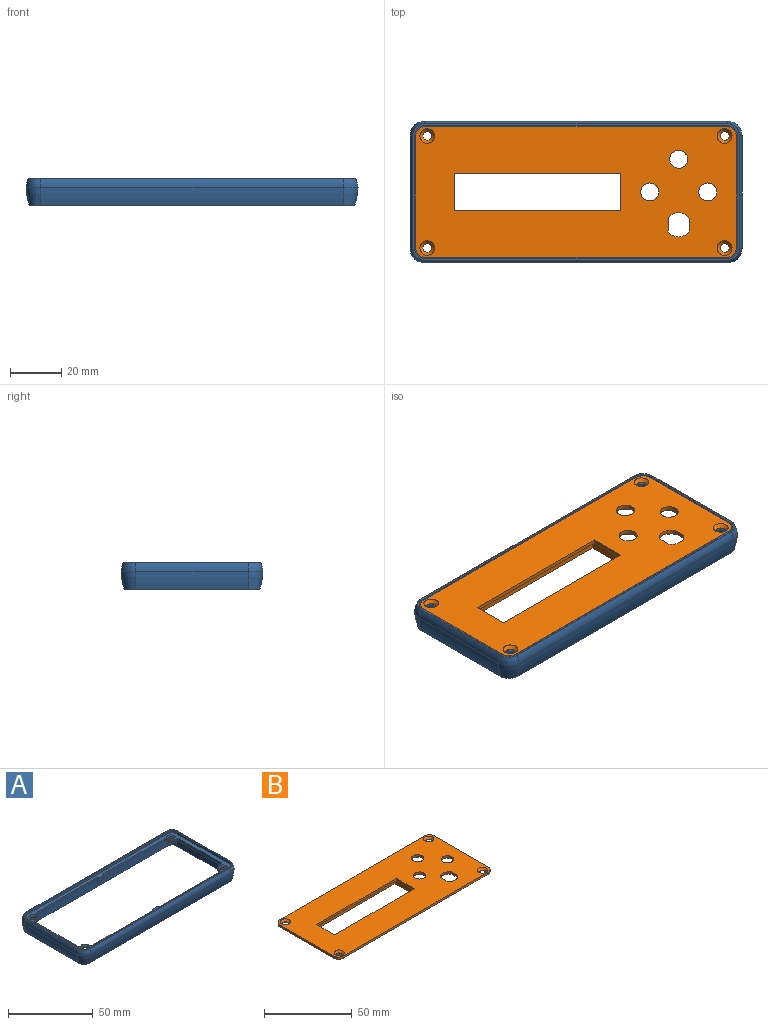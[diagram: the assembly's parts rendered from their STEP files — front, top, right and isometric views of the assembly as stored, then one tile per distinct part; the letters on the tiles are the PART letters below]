
ASSEMBLY  parts=2 mates=1
PART A: 104 faces, bbox 129.9x56.1x10.5 mm
  f0: torus R=5.55mm, axis (0,0,-1), area 0.1mm2, adj f4,f5,f68,f77
  f1: torus R=5.55mm, axis (0,0,-1), area 0.1mm2, adj f4,f6,f66,f94
  f2: torus R=5.55mm, axis (0,0,-1), area 0.1mm2, adj f5,f7,f75,f87
  f3: torus R=5.55mm, axis (0,0,-1), area 0.1mm2, adj f6,f7,f79,f90
  f4: cylinder r=0.2mm len=117.5mm, axis (1,0,0), area 1.3mm2, adj f0,f1,f67,f97
  f5: cylinder r=0.2mm len=43.63mm, axis (0,1,0), area 0.5mm2, adj f0,f2,f76,f102
  f6: cylinder r=0.2mm len=43.63mm, axis (0,-1,0), area 0.5mm2, adj f1,f3,f65,f92
  f7: cylinder r=0.2mm len=117.5mm, axis (-1,0,0), area 1.3mm2, adj f2,f3,f74,f80
  f8: cylinder r=0.2mm len=43.63mm, axis (0,-1,0), area 9.2mm2, adj f72,f73,f78,f92
  f9: cylinder r=0.2mm len=117.5mm, axis (-1,0,0), area 24.7mm2, adj f71,f73,f74,f78
  f10: cylinder r=0.2mm len=117.5mm, axis (1,0,0), area 24.7mm2, adj f70,f72,f78,f97
  f11: cylinder r=0.2mm len=43.63mm, axis (0,1,0), area 9.2mm2, adj f70,f71,f76,f78
  f12: cylinder r=0.2mm len=43.63mm, axis (0,-1,0), area 11mm2, adj f63,f64,f65,f69
  f13: cylinder r=0.2mm len=117.5mm, axis (-1,0,0), area 29.5mm2, adj f62,f64,f69,f80
  f14: cylinder r=0.2mm len=117.5mm, axis (1,0,0), area 29.5mm2, adj f61,f63,f67,f69
  f15: cylinder r=0.2mm len=43.63mm, axis (0,1,0), area 11mm2, adj f61,f62,f69,f102
  f16: cylinder r=1mm len=1.8mm, axis (0,0,-1), area 2.8mm2, adj f32,f54,f56,f85
  f17: cylinder r=1mm len=1.8mm, axis (0,0,1), area 2.8mm2, adj f32,f49,f55,f85
  f18: cylinder r=1mm len=1.8mm, axis (0,0,-1), area 2.8mm2, adj f32,f48,f55,f85
  f19: cylinder r=1mm len=1.8mm, axis (0,0,1), area 2.8mm2, adj f32,f45,f56,f85
  f20: cylinder r=1mm len=3mm, axis (0,0,-1), area 4.7mm2, adj f32,f35,f36,f37,f39
  f21: cylinder r=1mm len=3mm, axis (0,0,-1), area 4.7mm2, adj f32,f35,f36,f37,f40
  f22: cylinder r=1mm len=3mm, axis (0,0,-1), area 4.7mm2, adj f32,f33,f34,f38,f41
  f23: cylinder r=1mm len=3mm, axis (0,0,-1), area 4.7mm2, adj f32,f33,f34,f38,f42
  f24: cylinder r=1.75mm len=3.5mm, axis (0,0,-1), area 11.5mm2, adj f25,f85
  f25: cone r=2.12mm half-angle=45deg, axis (0,0,1), area 14.2mm2, adj f24,f32
  f26: cylinder r=1.75mm len=3.5mm, axis (0,0,-1), area 11.5mm2, adj f27,f85
  f27: cone r=2.12mm half-angle=45deg, axis (0,0,1), area 14.2mm2, adj f26,f32
  f28: cylinder r=1.75mm len=3.5mm, axis (0,0,-1), area 11.5mm2, adj f29,f85
  f29: cone r=2.12mm half-angle=45deg, axis (0,0,1), area 14.2mm2, adj f28,f32
  f30: cylinder r=1.75mm len=3.5mm, axis (0,0,-1), area 11.5mm2, adj f31,f85
  f31: cone r=2.12mm half-angle=45deg, axis (0,0,1), area 14.2mm2, adj f30,f32
  f32: plane 125.5x51.63mm, normal (0,0,1), area 816.8mm2, adj f16,f17,f18,f19,f20,f21,f22,f23
  f33: plane 5x1mm, normal (0,0,-1), area 4.6mm2, adj f22,f23,f34,f38
  f34: plane 3x3mm, normal (0,1,0), area 9mm2, adj f22,f23,f32,f33
  f35: plane 5x1mm, normal (0,0,-1), area 4.6mm2, adj f20,f21,f36,f37
  f36: plane 3x3mm, normal (0,-1,0), area 9mm2, adj f20,f21,f32,f35
  f37: plane 5x1.2mm, normal (0,1,0), area 6mm2, adj f20,f21,f35,f85
  f38: plane 5x1.2mm, normal (0,-1,0), area 6mm2, adj f22,f23,f33,f85
  f39: plane 51.26x1.8mm, normal (0,-1,0), area 92.3mm2, adj f20,f32,f50,f85
  f40: plane 51.26x1.8mm, normal (0,-1,0), area 92.3mm2, adj f21,f32,f43,f85
  f41: plane 51.26x1.8mm, normal (0,1,0), area 92.3mm2, adj f22,f32,f46,f85
  f42: plane 51.26x1.8mm, normal (0,1,0), area 92.3mm2, adj f23,f32,f52,f85
  f43: cylinder r=1mm len=1.8mm, axis (0,0,-1), area 2.8mm2, adj f32,f40,f44,f85
  f44: plane 1.8x0.81mm, normal (1,0,0), area 1.4mm2, adj f32,f43,f84,f85
  f45: plane 1.8x1.49mm, normal (0,1,0), area 2.7mm2, adj f19,f32,f81,f85
  f46: cylinder r=1mm len=1.8mm, axis (0,0,1), area 2.8mm2, adj f32,f41,f47,f85
  f47: plane 1.8x0.81mm, normal (1,0,0), area 1.4mm2, adj f32,f46,f82,f85
  f48: plane 1.8x1.49mm, normal (0,1,0), area 2.7mm2, adj f18,f32,f82,f85
  f49: plane 1.8x1.49mm, normal (0,-1,0), area 2.7mm2, adj f17,f32,f84,f85
  f50: cylinder r=1mm len=1.8mm, axis (0,0,1), area 2.8mm2, adj f32,f39,f51,f85
  f51: plane 1.8x0.81mm, normal (-1,0,0), area 1.4mm2, adj f32,f50,f83,f85
  f52: cylinder r=1mm len=1.8mm, axis (0,0,-1), area 2.8mm2, adj f32,f42,f53,f85
  f53: plane 1.8x0.81mm, normal (-1,0,0), area 1.4mm2, adj f32,f52,f81,f85
  f54: plane 1.8x1.49mm, normal (0,-1,0), area 2.7mm2, adj f16,f32,f83,f85
  f55: plane 35.52x1.8mm, normal (1,0,0), area 63.9mm2, adj f17,f18,f32,f85
  f56: plane 35.52x1.8mm, normal (-1,0,0), area 63.9mm2, adj f16,f19,f32,f85
  f57: cylinder r=4mm len=4mm, axis (0,0,-1), area 10.7mm2, adj f32,f58,f78,f96
  f58: plane 43.63x1.7mm, normal (-1,0,0), area 74.2mm2, adj f32,f57,f59,f78
  f59: cylinder r=4mm len=4mm, axis (0,0,-1), area 10.7mm2, adj f32,f58,f60,f78
  f60: plane 117.5x1.7mm, normal (0,1,0), area 199.8mm2, adj f32,f59,f78,f86
  f61: torus R=4.36mm, axis (0,0,-1), area 1.8mm2, adj f14,f15,f68,f69
  f62: torus R=4.36mm, axis (0,0,-1), area 1.8mm2, adj f13,f15,f69,f87
  f63: torus R=4.36mm, axis (0,0,-1), area 1.8mm2, adj f12,f14,f66,f69
  f64: torus R=4.36mm, axis (0,0,-1), area 1.8mm2, adj f12,f13,f69,f79
  f65: cylinder r=25mm len=43.63mm, axis (0,-1,0), area 304.7mm2, adj f6,f12,f66,f79
  f66: revolved ~6.86x5.75mm, area 58.2mm2, adj f1,f63,f65,f67
  f67: cylinder r=25mm len=117.5mm, axis (1,0,0), area 820.6mm2, adj f4,f14,f66,f68
  f68: revolved ~6.86x5.75mm, area 58.2mm2, adj f0,f61,f67,f102
  f69: plane 126.21x52.34mm, normal (0,0,-1), area 123.7mm2, adj f12,f13,f14,f15,f61,f62,f63,f64
  f70: torus R=4.63mm, axis (0,0,-1), area 1.6mm2, adj f10,f11,f77,f78
  f71: torus R=4.63mm, axis (0,0,-1), area 1.6mm2, adj f9,f11,f75,f78
  f72: torus R=4.63mm, axis (0,0,-1), area 1.6mm2, adj f8,f10,f78,f94
  f73: torus R=4.63mm, axis (0,0,-1), area 1.6mm2, adj f8,f9,f78,f90
  f74: cylinder r=7.19mm len=117.5mm, axis (-1,0,0), area 418mm2, adj f7,f9,f75,f90
  f75: revolved ~5.75x5.75mm, area 30.3mm2, adj f2,f71,f74,f76
  f76: cylinder r=7.19mm len=43.63mm, axis (0,1,0), area 155.2mm2, adj f5,f11,f75,f77
  f77: revolved ~5.75x5.75mm, area 30.3mm2, adj f0,f70,f76,f97
  f78: plane 126.77x52.9mm, normal (0,0,1), area 221.8mm2, adj f8,f9,f10,f11,f57,f58,f59,f60
  f79: revolved ~6.86x5.75mm, area 58.2mm2, adj f3,f64,f65,f80
  f80: cylinder r=25mm len=117.5mm, axis (-1,0,0), area 820.6mm2, adj f7,f13,f79,f87
  f81: cylinder r=3mm len=3mm, axis (0,0,-1), area 8.5mm2, adj f32,f45,f53,f85
  f82: cylinder r=3mm len=3mm, axis (0,0,-1), area 8.5mm2, adj f32,f47,f48,f85
  f83: cylinder r=3mm len=3mm, axis (0,0,-1), area 8.5mm2, adj f32,f51,f54,f85
  f84: cylinder r=3mm len=3mm, axis (0,0,-1), area 8.5mm2, adj f32,f44,f49,f85
  f85: plane 125.5x51.63mm, normal (0,0,-1), area 847.7mm2, adj f16,f17,f18,f19,f24,f26,f28,f30
  f86: cylinder r=4mm len=4mm, axis (0,0,-1), area 10.7mm2, adj f32,f60,f78,f101
  f87: revolved ~6.86x5.75mm, area 58.2mm2, adj f2,f62,f80,f102
  f88: cylinder r=4mm len=7mm, axis (0,0,-1), area 44mm2, adj f69,f85,f89,f103
  f89: plane 117.5x7mm, normal (0,1,0), area 822.5mm2, adj f69,f85,f88,f91
  f90: revolved ~5.75x5.75mm, area 30.3mm2, adj f3,f73,f74,f92
  f91: cylinder r=4mm len=7mm, axis (0,0,-1), area 44mm2, adj f69,f85,f89,f93
  f92: cylinder r=7.19mm len=43.63mm, axis (0,-1,0), area 155.2mm2, adj f6,f8,f90,f94
  f93: plane 43.63x7mm, normal (-1,0,0), area 305.4mm2, adj f69,f85,f91,f95
  f94: revolved ~5.75x5.75mm, area 30.3mm2, adj f1,f72,f92,f97
  f95: cylinder r=4mm len=7mm, axis (0,0,-1), area 44mm2, adj f69,f85,f93,f98
  f96: plane 117.5x1.7mm, normal (0,-1,0), area 199.8mm2, adj f32,f57,f78,f99
  f97: cylinder r=7.19mm len=117.5mm, axis (1,0,0), area 418mm2, adj f4,f10,f77,f94
  f98: plane 117.5x7mm, normal (0,-1,0), area 822.5mm2, adj f69,f85,f95,f100
  f99: cylinder r=4mm len=4mm, axis (0,0,-1), area 10.7mm2, adj f32,f78,f96,f101
  f100: cylinder r=4mm len=7mm, axis (0,0,-1), area 44mm2, adj f69,f85,f98,f103
  f101: plane 43.63x1.7mm, normal (1,0,0), area 74.2mm2, adj f32,f78,f86,f99
  f102: cylinder r=25mm len=43.63mm, axis (0,1,0), area 304.7mm2, adj f5,f15,f68,f87
  f103: plane 43.63x7mm, normal (1,0,0), area 305.4mm2, adj f69,f85,f88,f100
PART B: 82 faces, bbox 124.8x50.9x8 mm
  f0: plane 10.05x4mm, normal (1,0,0), area 40.2mm2, adj f56,f59,f75,f81
  f1: plane 71.5x24mm, normal (0,0,-1), area 780.8mm2, adj f28,f29,f30,f31,f43,f67,f68,f69
  f2: plane 0.49x0.01mm, normal (0,0,-1), area 0mm2, adj f44,f65
  f3: plane 1.2x0.12mm, normal (0,0,-1), area 0.1mm2, adj f5,f58
  f4: plane 13x12.9mm, normal (0,0,-1), area 93.5mm2, adj f34,f42,f61,f80,f81
  f5: cylinder r=2.5mm len=2.5mm, axis (0,0,1), area 2.9mm2, adj f3,f56,f58
  f6: cylinder r=2.5mm len=2.5mm, axis (0,0,1), area 1.2mm2, adj f56,f57
  f7: plane 13x13mm, normal (0,0,-1), area 94.2mm2, adj f33,f53
  f8: plane 124.8x50.9mm, normal (0,0,-1), area 1172.2mm2, adj f13,f15,f17,f19,f20,f21,f22,f23
  f9: plane 13x13mm, normal (0,0,-1), area 94.2mm2, adj f32,f52
  f10: plane 15.5x14.2mm, normal (0,0,-1), area 116.6mm2, adj f35,f36,f37,f38,f39,f40,f41,f55
  f11: plane 124.8x50.9mm, normal (0,0,1), area 5117.3mm2, adj f12,f14,f16,f18,f20,f21,f22,f23
  f12: cone r=2.31mm half-angle=41deg, axis (0,0,1), area 24.9mm2, adj f11,f13
  f13: cylinder r=1.75mm len=3.5mm, axis (0,0,1), area 1.7mm2, adj f8,f12
  f14: cone r=2.31mm half-angle=41deg, axis (0,0,1), area 24.9mm2, adj f11,f15
  f15: cylinder r=1.75mm len=3.5mm, axis (0,0,1), area 1.7mm2, adj f8,f14
  f16: cone r=2.31mm half-angle=41deg, axis (0,0,1), area 24.9mm2, adj f11,f17
  f17: cylinder r=1.75mm len=3.5mm, axis (0,0,1), area 1.7mm2, adj f8,f16
  f18: cone r=2.31mm half-angle=41deg, axis (0,0,1), area 24.9mm2, adj f11,f19
  f19: cylinder r=1.75mm len=3.5mm, axis (0,0,1), area 1.7mm2, adj f8,f18
  f20: plane 42.9x1.45mm, normal (-1,0,0), area 62.2mm2, adj f8,f11,f21,f27
  f21: cylinder r=4mm len=4mm, axis (0,0,-1), area 9.1mm2, adj f8,f11,f20,f22
  f22: plane 116.8x1.45mm, normal (0,-1,0), area 169.4mm2, adj f8,f11,f21,f23
  f23: cylinder r=4mm len=4mm, axis (0,0,-1), area 9.1mm2, adj f8,f11,f22,f24
  f24: plane 42.9x1.45mm, normal (1,0,0), area 62.2mm2, adj f8,f11,f23,f25
  f25: cylinder r=4mm len=4mm, axis (0,0,-1), area 9.1mm2, adj f8,f11,f24,f26
  f26: plane 116.8x1.45mm, normal (0,1,0), area 169.4mm2, adj f8,f11,f25,f27
  f27: cylinder r=4mm len=4mm, axis (0,0,-1), area 9.1mm2, adj f8,f11,f20,f26
  f28: plane 64.5x1.45mm, normal (0,1,0), area 93.5mm2, adj f1,f11,f29,f31
  f29: plane 14.5x1.45mm, normal (1,0,0), area 21mm2, adj f1,f11,f28,f30
  f30: plane 64.5x1.45mm, normal (0,-1,0), area 93.5mm2, adj f1,f11,f29,f31
  f31: plane 14.5x1.45mm, normal (-1,0,0), area 21mm2, adj f1,f11,f28,f30
  f32: cylinder r=3.5mm len=7mm, axis (0,0,1), area 31.9mm2, adj f9,f11
  f33: cylinder r=3.5mm len=7mm, axis (0,0,1), area 31.9mm2, adj f7,f11
  f34: cylinder r=3.5mm len=7mm, axis (0,0,1), area 31.9mm2, adj f4,f11
  f35: plane 4.8x1.45mm, normal (1,0,0), area 7mm2, adj f10,f11,f36,f38
  f36: cylinder r=4.75mm len=8.2mm, axis (0,0,1), area 14.3mm2, adj f10,f11,f35,f37
  f37: plane 4.8x1.45mm, normal (-1,0,0), area 7mm2, adj f10,f11,f36,f38
  f38: cylinder r=4.75mm len=8.2mm, axis (0,0,1), area 14.3mm2, adj f10,f11,f35,f37
  f39: plane 6.21x2.5mm, normal (-1,0,0), area 15.5mm2, adj f10,f40,f55,f56
  f40: cylinder r=7.75mm len=14.2mm, axis (0,0,1), area 44.9mm2, adj f10,f39,f41,f56
  f41: plane 6.21x2.5mm, normal (1,0,0), area 15.5mm2, adj f10,f40,f55,f56
  f42: cylinder r=6.5mm len=13mm, axis (0,0,1), area 69.6mm2, adj f4,f56,f61,f80
  f43: plane 24x6.5mm, normal (1,0,0), area 82mm2, adj f1,f56,f66,f67,f69,f74,f75
  f44: cylinder r=2.5mm len=2.5mm, axis (0,0,1), area 1.2mm2, adj f2,f56,f65
  f45: cylinder r=2.95mm len=4.09mm, axis (0,0,1), area 15mm2, adj f8,f46,f54,f56
  f46: plane 109.63x2.5mm, normal (0,-1,0), area 274.1mm2, adj f8,f45,f47,f56
  f47: cylinder r=2.95mm len=4.09mm, axis (0,0,1), area 15mm2, adj f8,f46,f48,f56
  f48: plane 38.08x2.5mm, normal (-1,0,0), area 95.2mm2, adj f8,f47,f49,f56
  f49: cylinder r=2.95mm len=4.09mm, axis (0,0,1), area 15mm2, adj f8,f48,f50,f56
  f50: plane 109.63x2.5mm, normal (0,1,0), area 274.1mm2, adj f8,f49,f51,f56
  f51: cylinder r=2.95mm len=4.09mm, axis (0,0,1), area 15mm2, adj f8,f50,f54,f56
  f52: cylinder r=6.5mm len=13mm, axis (0,0,1), area 102.1mm2, adj f9,f56
  f53: cylinder r=6.5mm len=13mm, axis (0,0,1), area 102.1mm2, adj f7,f56
  f54: plane 38.08x2.5mm, normal (1,0,0), area 95.2mm2, adj f8,f45,f51,f56
  f55: cylinder r=7.75mm len=14.2mm, axis (0,0,1), area 44.9mm2, adj f10,f39,f41,f56
  f56: plane 117.81x43.91mm, normal (0,0,-1), area 1778.4mm2, adj f0,f5,f6,f39,f40,f41,f42,f43
  f57: plane 6.53x6.52mm, normal (-1,0,0), area 27.2mm2, adj f6,f56,f60,f74,f75
  f58: plane 74.93x6.5mm, normal (0,1,0), area 302.6mm2, adj f3,f5,f56,f59,f60,f75
  f59: cylinder r=2.5mm len=4mm, axis (0,0,1), area 13.1mm2, adj f0,f56,f58,f75
  f60: cylinder r=2.5mm len=4mm, axis (0,0,1), area 17.4mm2, adj f56,f57,f58,f75
  f61: plane 10.07x6.5mm, normal (1,0,0), area 40.3mm2, adj f4,f42,f56,f62,f75,f81
  f62: cylinder r=2.5mm len=4mm, axis (0,0,1), area 15.7mm2, adj f56,f61,f63,f75
  f63: plane 74.77x4mm, normal (0,-1,0), area 299.1mm2, adj f56,f62,f64,f75
  f64: cylinder r=2.5mm len=4mm, axis (0,0,1), area 15.6mm2, adj f56,f63,f65,f75
  f65: plane 6.5x6.5mm, normal (-1,0,0), area 27.2mm2, adj f2,f44,f56,f64,f66,f75
  f66: plane 4.24x4mm, normal (0,1,0), area 17mm2, adj f43,f56,f65,f75
  f67: plane 71.5x6.5mm, normal (0,1,0), area 464.8mm2, adj f1,f43,f68,f75
  f68: plane 24x6.5mm, normal (-1,0,0), area 156mm2, adj f1,f67,f69,f75
  f69: plane 71.5x6.5mm, normal (0,-1,0), area 464.8mm2, adj f1,f43,f68,f75
  f70: cylinder r=1.25mm len=6.5mm, axis (0,0,1), area 51.1mm2, adj f75,f79
  f71: cylinder r=1.25mm len=6.5mm, axis (0,0,1), area 51.1mm2, adj f75,f78
  f72: cylinder r=1.25mm len=6.5mm, axis (0,0,1), area 51.1mm2, adj f75,f77
  f73: cylinder r=1.25mm len=6.5mm, axis (0,0,1), area 51.1mm2, adj f75,f76
  f74: plane 4.24x4mm, normal (0,-1,0), area 17mm2, adj f43,f56,f57,f75
  f75: plane 79.99x36.04mm, normal (0,0,-1), area 1033.1mm2, adj f0,f43,f57,f58,f59,f60,f61,f62
  f76: plane 2.5x2.5mm, normal (0,0,-1), area 4.9mm2, adj f73
  f77: plane 2.5x2.5mm, normal (0,0,-1), area 4.9mm2, adj f72
  f78: plane 2.5x2.5mm, normal (0,0,-1), area 4.9mm2, adj f71
  f79: plane 2.5x2.5mm, normal (0,0,-1), area 4.9mm2, adj f70
  f80: plane 2.5x0.05mm, normal (-1,0,0), area 0.1mm2, adj f4,f42,f56,f81
  f81: cylinder r=6.65mm len=10.96mm, axis (0,0,-1), area 83.8mm2, adj f0,f4,f61,f75,f80
PLACE A t=(14.95,1.99,-5.99)mm
PLACE B t=(55.21,13.56,-2.74)mm
MATE fastened B.f14 <-> A.f29  axis (0,0,-1) through (112.97,35.32,-4.19)mm
